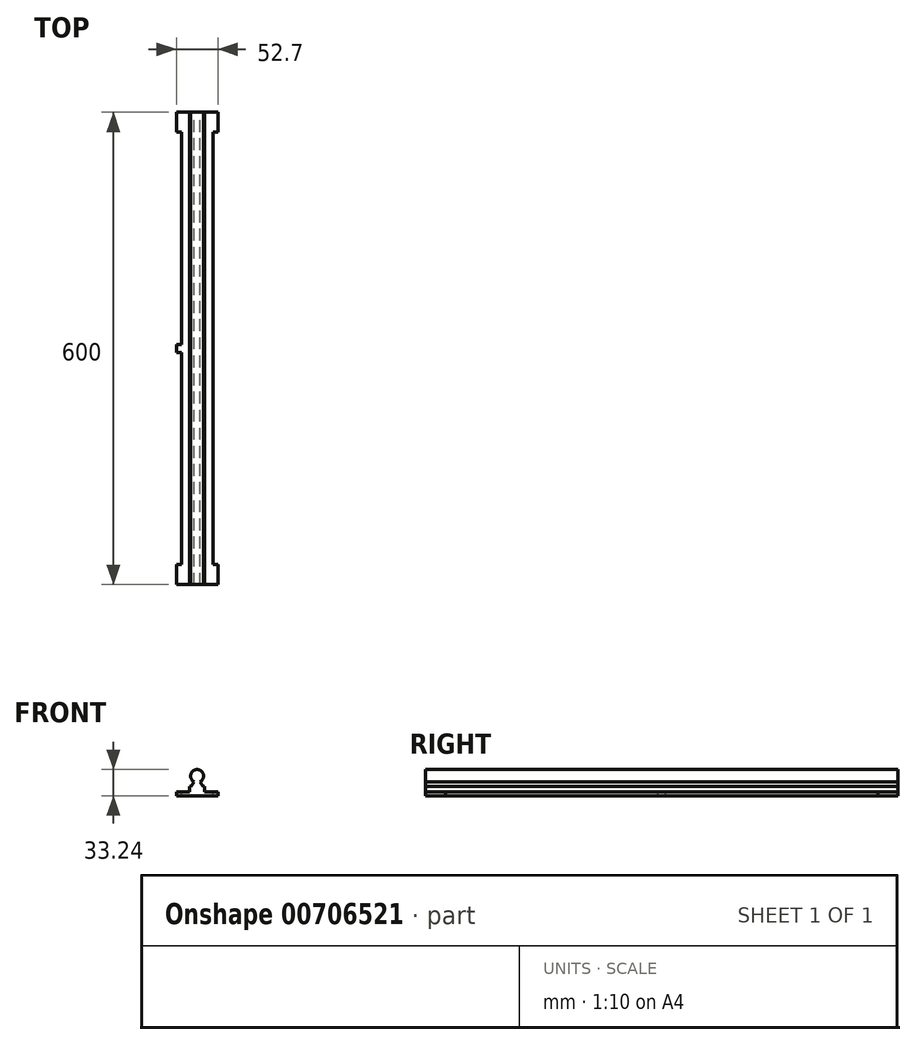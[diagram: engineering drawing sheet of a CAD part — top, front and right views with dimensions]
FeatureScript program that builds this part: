
annotation { "Feature Type Name" : "Feature", "Feature Type Description" : "" }
export const myFeature = defineFeature(function(context is Context, id is Id, definition is map)
    precondition{}
    {
        {
            var Q0;
            Q0=qCreatedBy(makeId("Front.planeOp"),FACE);
            var sketch = newSketch(context, id + "F0", { "sketchPlane" : qUnion([Q0])});
            skLineSegment(sketch, "E0", {"start": v(0, 0) * mm, "end": v(-40, 0) * mm});
            skLineSegment(sketch, "E1", {"start": v(-40, 0) * mm, "end": v(-40, 5) * mm});
            skLineSegment(sketch, "E2", {"start": v(0, 0) * mm, "end": v(0, 5) * mm});
            skLineSegment(sketch, "E3", {"start": v(-40, 5) * mm, "end": v(-29.25, 5) * mm});
            skLineSegment(sketch, "E4", {"start": v(0, 5) * mm, "end": v(-10.75, 5) * mm});
            skLineSegment(sketch, "E5", {"start": v(-29.25, 5) * mm, "end": v(-29.25, 11.7) * mm});
            skLineSegment(sketch, "E6", {"start": v(-10.75, 5) * mm, "end": v(-10.75, 11.7) * mm});
            skLineSegment(sketch, "E7", {"start": v(-10.75, 11.7) * mm, "end": v(-12.48, 11.7) * mm});
            skLineSegment(sketch, "E8", {"start": v(-12.48, 11.7) * mm, "end": v(-16, 17.8) * mm});
            skLineSegment(sketch, "E9", {"start": v(-29.25, 11.7) * mm, "end": v(-27.52, 11.7) * mm});
            skLineSegment(sketch, "E10", {"start": v(-27.52, 11.7) * mm, "end": v(-24, 17.8) * mm});
            skArc(sketch, "E11", {"start": v(-16, 17.8) * mm, "mid": v(-20, 33.24) * mm, "end": v(-24, 17.8) * mm});
            skSolve(sketch);
        }
        {
            var Q0;
            Q0 = qSketchRegion(id + "F0", true);
            extrude(context, id + "F1", {"entities" : qUnion([Q0]), "depth" : 600 * mm, "offsetDistance" : 25.4 * mm});
        }
        {
            var Q0;
            Q0=makeQuery(id+"F1.opExtrude","SWEPT_FACE",FACE,{"disambiguationData":[OSD([sQuery(id+"F0.wireOp",EDGE,"E3")])]});
            var sketch = newSketch(context, id + "F2", { "sketchPlane" : qUnion([Q0])});
            skLineSegment(sketch, "E12.bottom", {"start": v(-46.35, -574.6) * mm, "end": v(6.35, -574.6) * mm});
            skLineSegment(sketch, "E12.top", {"start": v(-46.35, -600) * mm, "end": v(6.35, -600) * mm});
            skLineSegment(sketch, "E12.left", {"start": v(-46.35, -574.6) * mm, "end": v(-46.35, -600) * mm});
            skLineSegment(sketch, "E12.right", {"start": v(6.35, -574.6) * mm, "end": v(6.35, -600) * mm});
            skLineSegment(sketch, "E13.bottom", {"start": v(-46.35, 0) * mm, "end": v(6.35, 0) * mm});
            skLineSegment(sketch, "E13.top", {"start": v(-46.35, -25.4) * mm, "end": v(6.35, -25.4) * mm});
            skLineSegment(sketch, "E13.left", {"start": v(-46.35, 0) * mm, "end": v(-46.35, -25.4) * mm});
            skLineSegment(sketch, "E13.right", {"start": v(6.35, 0) * mm, "end": v(6.35, -25.4) * mm});
            skSolve(sketch);
        }
        {
            var Q0;
            Q0 = qSketchRegion(id + "F2", true);
            var Q1;
            Q1=makeQuery(id+"F1.opExtrude","SWEPT_FACE",FACE,{"disambiguationData":[OSD([sQuery(id+"F0.wireOp",EDGE,"E0")])]});
            extrude(context, id + "F3", {"entities" : qUnion([Q0]), "operationType" : NewBodyOperationType.ADD, "endBound" : BoundingType.UP_TO_SURFACE, "oppositeDirection" : true, "depth" : 25.4 * mm, "endBoundEntityFace" : qUnion([Q1]), "offsetDistance" : 25.4 * mm});
        }
        {
            var Q0;
            Q0=makeQuery(id+"F3.boolean.opBoolean","MERGE",FACE,{"derivedFrom":[makeQuery(id+"F1.opExtrude","SWEPT_FACE",FACE,{"disambiguationData":[OSD([sQuery(id+"F0.wireOp",EDGE,"E3")])]}),makeQuery(id+"F3.opExtrude","CAP_FACE",FACE,{"disambiguationData":[OSD([sQuery(id+"F2.wireOp",EDGE,"E12.bottom"),sQuery(id+"F2.wireOp",EDGE,"E12.top"),sQuery(id+"F2.wireOp",EDGE,"E12.left"),sQuery(id+"F2.wireOp",EDGE,"E12.right")])],"isStart":true}),makeQuery(id+"F3.opExtrude","CAP_FACE",FACE,{"disambiguationData":[OSD([sQuery(id+"F2.wireOp",EDGE,"E13.bottom"),sQuery(id+"F2.wireOp",EDGE,"E13.top"),sQuery(id+"F2.wireOp",EDGE,"E13.left"),sQuery(id+"F2.wireOp",EDGE,"E13.right")])],"isStart":true})]});
            var sketch = newSketch(context, id + "F4", { "sketchPlane" : qUnion([Q0])});
            skLineSegment(sketch, "E14.bottom", {"start": v(-40, -295) * mm, "end": v(-46.35, -295) * mm});
            skLineSegment(sketch, "E14.top", {"start": v(-40, -305) * mm, "end": v(-46.35, -305) * mm});
            skLineSegment(sketch, "E14.left", {"start": v(-40, -295) * mm, "end": v(-40, -305) * mm});
            skLineSegment(sketch, "E14.right", {"start": v(-46.35, -295) * mm, "end": v(-46.35, -305) * mm});
            skSolve(sketch);
        }
        {
            var Q0;
            Q0 = qSketchRegion(id + "F4", true);
            var Q1;
            {var subQ0=sQuery(id+"F0.wireOp",EDGE,"E0");Q1=makeQuery(id+"F3.boolean.opBoolean","MERGE",FACE,{"derivedFrom":[makeQuery(id+"F1.opExtrude","SWEPT_FACE",FACE,{"disambiguationData":[OSD([subQ0])]}),makeQuery(id+"F3.opExtrude","CAP_FACE",FACE,{"disambiguationData":[OSD([subQ0]),OD(0.0)],"isStart":false}),makeQuery(id+"F3.opExtrude","CAP_FACE",FACE,{"disambiguationData":[OSD([subQ0]),OD(1.0)],"isStart":false})]});}
            extrude(context, id + "F5", {"entities" : qUnion([Q0]), "operationType" : NewBodyOperationType.ADD, "endBound" : BoundingType.UP_TO_SURFACE, "oppositeDirection" : true, "depth" : 25.4 * mm, "endBoundEntityFace" : qUnion([Q1]), "offsetDistance" : 25.4 * mm});
        }
    });
